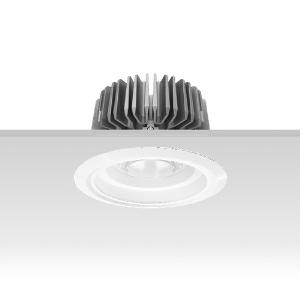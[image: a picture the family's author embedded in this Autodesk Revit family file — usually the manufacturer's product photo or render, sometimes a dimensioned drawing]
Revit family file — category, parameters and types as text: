
# Revit family: 3f_filippi_-_3f_reno_bianco_ampio_3f_filippi_-_30366_a01023_-_3f_reno_150_wh_3000-840_ep_wide___vt_wh_d195
name_source: partatom
category: Lighting Fixtures
units: mm (PartAtom-declared; Revit-internal decimal feet)

## family parameters
Cut with Voids When Loaded = No
Host = Face
Light Source = No
Part Type = Normal
Room Calculation Point = No
Round Connector Dimension = Use Diameter
Shared = No

## types (1)
- 3F Filippi - 3F Reno Bianco Ampio (1 x LED, 2647 lm, 29 W, 4000 K)
    Apparent Load = 29 VA
    Approval mark = ENEC
    CIE Flux Codes = 74 93 99 100 100
    Color Rendering = 80
    Color Temperature = 4000 K
    Control Gear = Electronic ballast
    Default Elevation = 1800 mm
    Description = ILLUMINOTECHNICAL
Luminous efficiency 100% (DLOR 100%, ULOR 0%).
Initial luminous flux of the luminaire 2647 lm.
Emergency luminaire luminous flux BLF 14.3%.
Direct symmetric wide distribution.
Installation Interdistance Transv.D = 1.54 x hu - Long.D = 1.54 x hu.
Tabular UGR (CIE 117 - 4H-8H; S=0.25H; 70/50/20): RUG 24.4 - 24.2.
Beam angle: 74° - 73°.
Luminous efficacy 91 lm/W.
Lifetime (L90/B10): 30000 h. (tq+25°C)
Lifetime (L85/B10): 50000 h. (tq+25°C)
Lifetime (L70/B10): 80000 h. (tq+25°C)
Sudden decreased luminous flux after 50000 hours: 0% (C0).
Photobiological safety in compliance with IEC/TR 62778: RG0 risk exempt, (IEC 62471).
In compliance with IEC/EN 62722-2-1 - IEC/EN 62717 standards.

SOURCE
Compact LED module 3000/840.
Energy efficiency class (UE 2019/2020 - UE 2019/2015): D.
CIE 13.3 Colour rendering index: CRI >80 (R9 <50%).
IES TM-30 Fidelity Index: Rf = 84 Rg = 95.
CCT nominal colour temperature 4000 K.
Colour initial tolerance (MacAdam): SDCM 3.
Zhaga Book 3 compliant.

MECHANICAL
Passive heat dissipator in die-casting aluminium, oversized, for optimum thermal management of the LED module.
Parabolic element with graduated/concentric rings in white polycarbonate.
Transparent external lens with glossy and satin differentiated surfaces, with a cooling and anti-insect system in methacrylate (PMMA).
Fastening spring clips in stainless steel.
Dimensions: diameter 176 mm, height 111 mm. Weight 2 kg.
IP44 protection degree for exposed part, IP20 for recessed part.
Mechanical strength to impacts IK06 (1 joule).
Glow-wire test resistance 650°C.

ELECTRICAL
Wiring on a separate unit.
Halogen Free electronic wiring 230V-50/60Hz, power factor 0.90, THD <25%, constant output current, SELV, class II, 1 driver.
Power of the luminaire 29 W.
CE - IEC 60598-1 - EN 60598-1.
EP maintained emergency wiring on board, 1h duration, 24h recharge; compliant with EN 60598-2-22, excluding high risk areas.
SAFE FLICKER: PstLM=<1 and SVM=<0.4 (IEC TR 61547-1 and IEC TR 63158), to ensure a more comfortable and safe light.
Ambient temperature from +5°C to +25°C.
Temperature class T6 max 85°C.
Relative humidity UR: <85%.

INSTALLATION
Pull-up recessed fitting.
False ceiling carving: 150 mm.
All accessories dedicated to this product are available on the Catalog and on our website www.3F-Filippi.com.

ACCESSORIES
A01023 - VT transparent glass, tempered, not flammable, locked and in line with the trim, in white polycarbonate.

APPLICATIONS
Environments: architectural, commercial, exhibition areas, transit areas, corridors, shops, display windows, service areas.
In false ceilings with narrow voids.

WARNING
Luminaire designed for disposal/recycling at end-of-life.
Replaceable (LED only) light source by a professional. Replaceable control gear by a professional.
    Height = 0 mm  [stored 0 ft]
    Lamp = 1 x LED
    Lamp Light Flux = 2647 lm
    Lamp Power = 29 W
    Lamp count = 1
    Length = 176 mm
    Lifetime = 50000 h
    Luminous efficacy = 91 lm/W
    Manufacturer = 3F Filippi
    ModVariant = No
    Model = 3F Filippi - 30366+A01023 - 3F Reno 150 WH 3000-840 EP WIDE + VT WH
    Mounting Place = Ceiling
    Mounting Type = Recessed
    Number of Poles = 1
    OnlyDefault = Yes
    Power Factor = 1
    Product Name = 3F Filippi - 3F Reno Bianco Ampio
    Product group = recessed luminaire
    ProductGroupID = 4
    Protection Class = Protection class II
    Protection Degree = IP 20
    RLX_Detail_Level = 1
    RLX_Emergency_Light_Flux = 0 lm
    RLX_Emergency_Type = 0
    RLX_Emergency_Type_DB = No
    RlxData = <blob elided: 84877 chars, md5=084a8d13>
    Socket = socket
    Standby Power = 0 W
    System Light Flux = 2647 lm
    System Power = 29 W
    Type Comments = Product without accessories
    Type Image = 3ffilippi_3f_reno_150_wh_d150__a01023.jpg
    URL = http://relux.com
    VarID = ---
    Voltage = 0 V
    Weight = 0.00 kg
    Width = 0 mm  [stored 0 ft]

note: [stored X ft] marks values corroborated as IEEE doubles in the binary element streams (Revit-internal decimal feet)

## geometry (parser evidence)
native form markers: Blend x4, Sweep x12
no freeform markers — native parametric forms only
